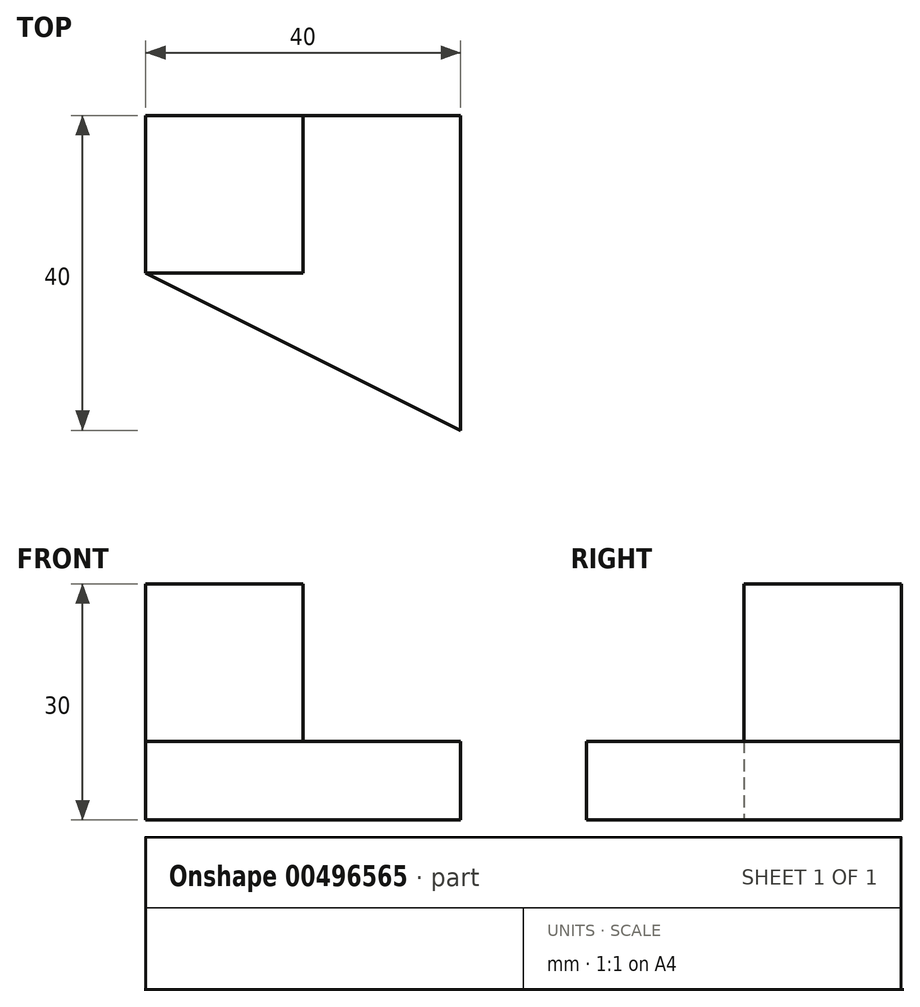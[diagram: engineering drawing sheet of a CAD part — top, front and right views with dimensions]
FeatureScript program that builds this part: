
annotation { "Feature Type Name" : "Feature", "Feature Type Description" : "" }
export const myFeature = defineFeature(function(context is Context, id is Id, definition is map)
    precondition{}
    {
        {
            var Q0;
            Q0=qCreatedBy(makeId("Top.planeOp"),FACE);
            var sketch = newSketch(context, id + "F0", { "sketchPlane" : qUnion([Q0])});
            skLineSegment(sketch, "E0", {"start": v(0, 0) * mm, "end": v(0, 20) * mm});
            skLineSegment(sketch, "E1", {"start": v(0, 20) * mm, "end": v(40, 20) * mm});
            skLineSegment(sketch, "E2", {"start": v(40, 20) * mm, "end": v(40, -20) * mm});
            skLineSegment(sketch, "E3", {"start": v(40, -20) * mm, "end": v(0, 0) * mm});
            skSolve(sketch);
        }
        {
            var Q0;
            Q0=makeQuery(id+"F0.imprint","IMPRINT",FACE,{"disambiguationData":[TD([[makeQuery(id+"F0.imprint","IMPRINT",EDGE,{"derivedFrom":sQuery(id+"F0.wireOp",EDGE,"E0")}),-1.0]])]});
            extrude(context, id + "F1", {"entities" : qUnion([Q0]), "depth" : 10 * mm});
        }
        {
            var Q0;
            Q0=makeQuery(id+"F1.opExtrude","CAP_FACE",FACE,{"disambiguationData":[OSD([sQuery(id+"F0.wireOp",EDGE,"E0"),sQuery(id+"F0.wireOp",EDGE,"E1"),sQuery(id+"F0.wireOp",EDGE,"E2"),sQuery(id+"F0.wireOp",EDGE,"E3")])],"isStart":false});
            var sketch = newSketch(context, id + "F2", { "sketchPlane" : qUnion([Q0])});
            skLineSegment(sketch, "E4", {"start": v(0, 20) * mm, "end": v(20, 20) * mm});
            skLineSegment(sketch, "E5", {"start": v(20, 20) * mm, "end": v(20, 0) * mm});
            skLineSegment(sketch, "E6", {"start": v(20, 0) * mm, "end": v(0, 0) * mm});
            skSolve(sketch);
        }
        {
            var Q0;
            Q0=makeQuery(id+"F2.imprint","IMPRINT",FACE,{"disambiguationData":[TD([[makeQuery(id+"F2.imprint","IMPRINT",EDGE,{"derivedFrom":sQuery(id+"F2.wireOp",EDGE,"E4")}),-1.0]])]});
            extrude(context, id + "F3", {"entities" : qUnion([Q0]), "operationType" : NewBodyOperationType.ADD, "depth" : 20 * mm});
        }
    });
